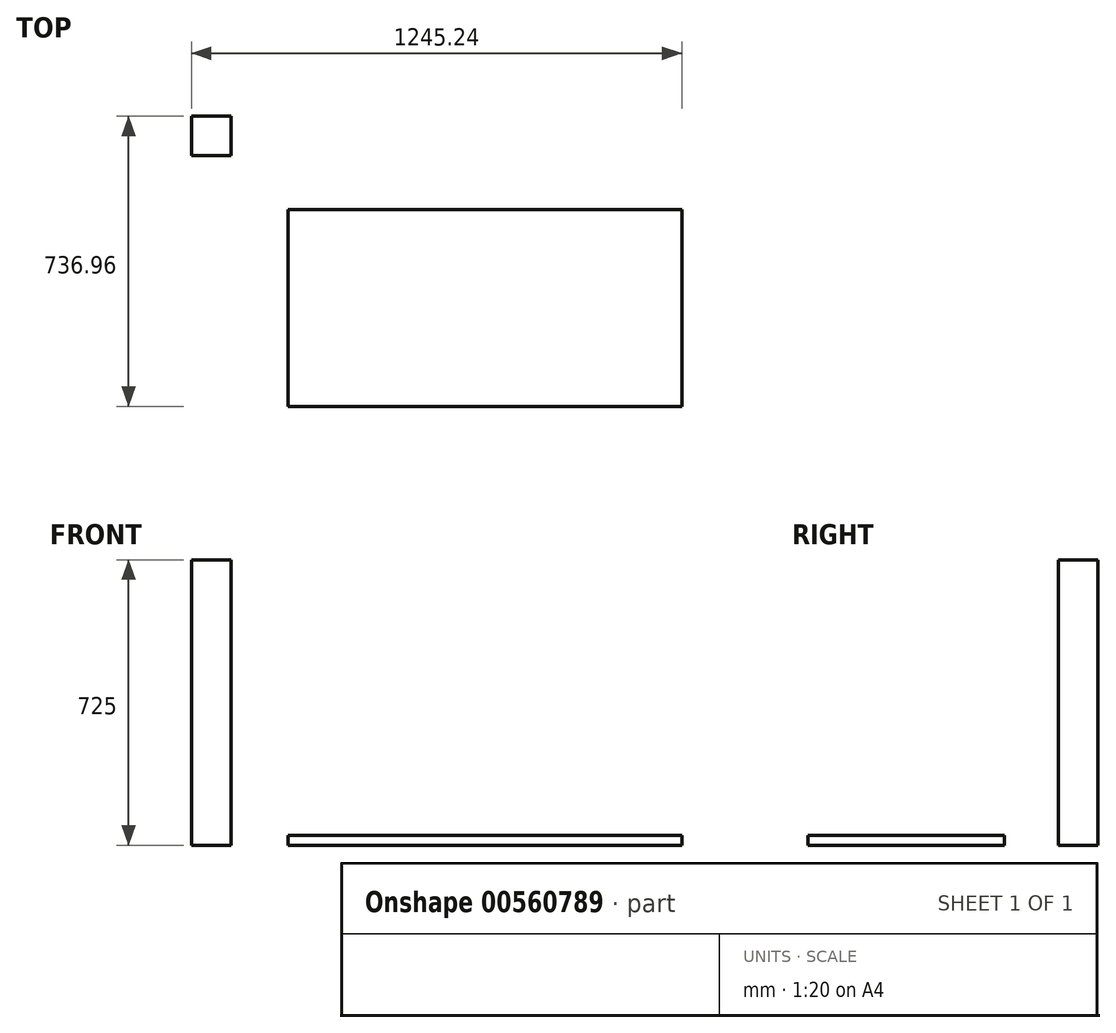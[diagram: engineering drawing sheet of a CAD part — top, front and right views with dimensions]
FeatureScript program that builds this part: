
annotation { "Feature Type Name" : "Feature", "Feature Type Description" : "" }
export const myFeature = defineFeature(function(context is Context, id is Id, definition is map)
    precondition{}
    {
        {
            var Q0;
            Q0=qCreatedBy(makeId("Top.planeOp"),FACE);
            var sketch = newSketch(context, id + "F0", { "sketchPlane" : qUnion([Q0])});
            skLineSegment(sketch, "E0.bottom", {"start": v(0, 0) * mm, "end": v(1000, 0) * mm});
            skLineSegment(sketch, "E0.top", {"start": v(0, 500) * mm, "end": v(1000, 500) * mm});
            skLineSegment(sketch, "E0.left", {"start": v(0, 0) * mm, "end": v(0, 500) * mm});
            skLineSegment(sketch, "E0.right", {"start": v(1000, 0) * mm, "end": v(1000, 500) * mm});
            skSolve(sketch);
        }
        {
            var Q0;
            Q0=makeQuery(id+"F0.imprint","IMPRINT",FACE,{"disambiguationData":[TD([[makeQuery(id+"F0.imprint","IMPRINT",EDGE,{"derivedFrom":sQuery(id+"F0.wireOp",EDGE,"E0.bottom")}),1.0]])]});
            var Q1;
            Q1=makeQuery(id+"F0.imprint","IMPRINT",FACE,{"disambiguationData":[TD([[makeQuery(id+"F0.imprint","IMPRINT",EDGE,{"derivedFrom":sQuery(id+"F0.wireOp",EDGE,"E0.bottom")}),1.0]])]});
            extrude(context, id + "F1", {"entities" : qUnion([Q0, Q1]), "depth" : 25 * mm, "offsetDistance" : 25 * mm});
        }
        {
            var Q0;
            Q0=qCreatedBy(makeId("Top.planeOp"),FACE);
            var sketch = newSketch(context, id + "F2", { "sketchPlane" : qUnion([Q0])});
            skLineSegment(sketch, "E1.bottom", {"start": v(-245.24, 636.96) * mm, "end": v(-145.24, 636.96) * mm});
            skLineSegment(sketch, "E1.top", {"start": v(-245.24, 736.96) * mm, "end": v(-145.24, 736.96) * mm});
            skLineSegment(sketch, "E1.left", {"start": v(-245.24, 636.96) * mm, "end": v(-245.24, 736.96) * mm});
            skLineSegment(sketch, "E1.right", {"start": v(-145.24, 636.96) * mm, "end": v(-145.24, 736.96) * mm});
            skSolve(sketch);
        }
        {
            var Q0;
            Q0 = qSketchRegion(id + "F2", true);
            extrude(context, id + "F3", {"entities" : qUnion([Q0]), "depth" : 725 * mm, "offsetDistance" : 25 * mm});
        }
    });
